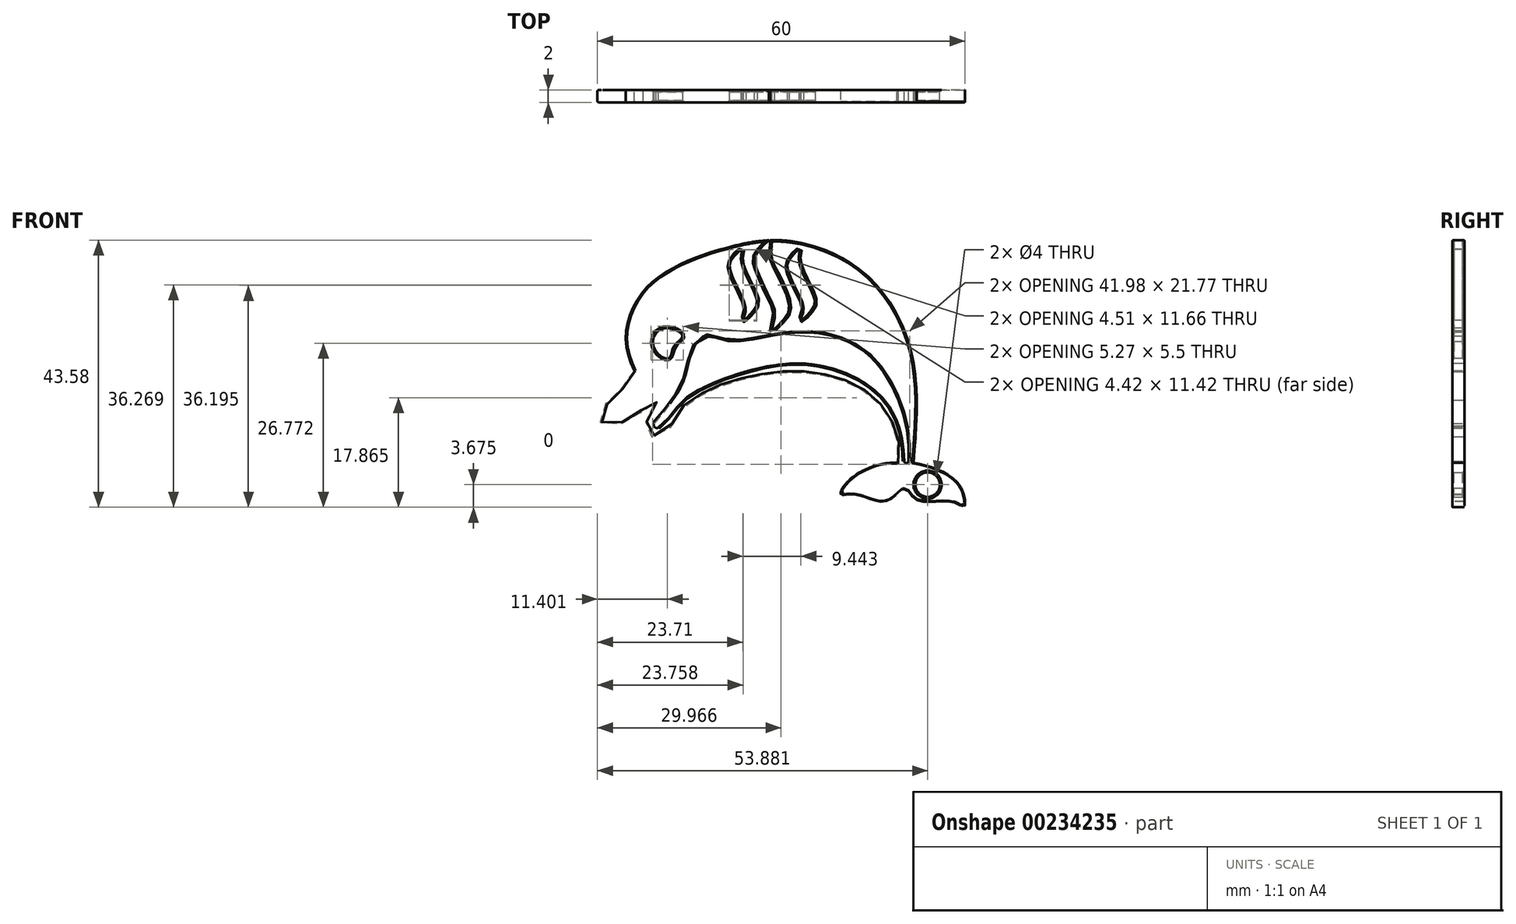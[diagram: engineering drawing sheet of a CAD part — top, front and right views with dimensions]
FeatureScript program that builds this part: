
annotation { "Feature Type Name" : "Feature", "Feature Type Description" : "" }
export const myFeature = defineFeature(function(context is Context, id is Id, definition is map)
    precondition{}
    {
        {
            var Q0;
            Q0=qCreatedBy(makeId("Front.planeOp"),FACE);
            var sketch = newSketch(context, id + "F0", { "sketchPlane" : qUnion([Q0])});
            skFitSpline(sketch, "E0", {"points": [v(-25.48, -7.62) * mm, v(-26.83, -2.44) * mm, v(-23.22, 6.13) * mm, v(-10.52, 12.36) * mm, v(0, 13.5) * mm, v(12.02, 8.3) * mm, v(19.83, -4.92) * mm, v(20.13, -22.67) * mm], "startDerivative": vector(-20.96, 49.8) * mm, "endDerivative": vector(-8.27, -104.1) * mm});
            skFitSpline(sketch, "E1", {"points": [v(20.13, -22.67) * mm, v(25.04, -24.25) * mm, v(28.1, -27.22) * mm, v(28.4, -29.9) * mm, v(26.81, -29.13) * mm, v(20.58, -28.67) * mm, v(18.7, -26.86) * mm, v(15.8, -28.9) * mm, v(10.31, -27.8) * mm, v(8.28, -27.87) * mm, v(9.54, -25.64) * mm, v(17.45, -22.67) * mm], "startDerivative": vector(47.96, -7.58) * mm, "endDerivative": vector(65.5, -3.83) * mm});
            skFitSpline(sketch, "E2", {"points": [v(17.45, -22.67) * mm, v(17.45, -18.89) * mm, v(13.41, -11.98) * mm, v(0.56, -7.9) * mm, v(-10.45, -9.84) * mm, v(-13.1, -10.91) * mm, v(-17.69, -13.98) * mm, v(-19.69, -17.15) * mm, v(-22.7, -18.48) * mm, v(-24.03, -17.48) * mm, v(-21.95, -12.6) * mm, v(-25.5, -15.24) * mm, v(-30.5, -16.46) * mm, v(-31.4, -14.6) * mm, v(-29.09, -12.24) * mm, v(-25.48, -7.62) * mm], "startDerivative": vector(8.68, 59.04) * mm, "endDerivative": vector(47.2, 70.58) * mm});
            skFitSpline(sketch, "E3", {"points": [v(-9.13, 12.73) * mm, v(-6.32, 19.23) * mm, v(-1.91, 23.13) * mm, v(0.96, 22.9) * mm, v(0, 20.55) * mm, v(0, 13.5) * mm], "startDerivative": vector(9.74, 28.22) * mm, "endDerivative": vector(4.25, -32.67) * mm});
            skFitSpline(sketch, "E4", {"points": [v(-19.86, -5.63) * mm, v(-22.28, -3.76) * mm, v(-20.8, -0.77) * mm, v(-17.55, -1.97) * mm, v(-18.89, -3.54) * mm, v(-19.86, -5.63) * mm]});
            skFitSpline(sketch, "E5", {"points": [v(-21.48, -16.92) * mm, v(-19.29, -14.65) * mm, v(-16.83, -11.98) * mm, v(-4.55, -7.12) * mm, v(6.9, -7.28) * mm, v(15.54, -12.61) * mm, v(18.6, -22.41) * mm], "startDerivative": vector(18.5, 14.45) * mm, "endDerivative": vector(1.69, -62.94) * mm});
            skFitSpline(sketch, "E6", {"points": [v(-22.23, -16.28) * mm, v(-17.9, -10.45) * mm, v(-16.42, -5.68) * mm, v(-14.3, -2.06) * mm, v(-9.93, -2.8) * mm, v(0, -1.47) * mm, v(12.5, -4.77) * mm, v(18.89, -16.33) * mm, v(19.3, -22.41) * mm], "startDerivative": vector(23.26, 24.72) * mm, "endDerivative": vector(-1, -48.83) * mm});
            skArc(sketch, "E7", {"start": v(-22.23, -16.28) * mm, "mid": v(-22.1, -16.88) * mm, "end": v(-21.48, -16.92) * mm});
            skArc(sketch, "E8", {"start": v(18.6, -22.41) * mm, "mid": v(18.95, -22.75) * mm, "end": v(19.3, -22.41) * mm});
            skCircle(sketch, "E9", {"center": v(22.43, -26.25) * mm, "radius": 2 * mm});
            skFitSpline(sketch, "E10", {"points": [v(-5.51, 11.36) * mm, v(-3.34, 13.68) * mm, v(-3.24, 13.56) * mm, v(-3.4, 12.14) * mm, v(-3.16, 10.16) * mm, v(-2.05, 7.9) * mm, v(-0.15, 3) * mm, v(-0.89, 0.9) * mm, v(-2.95, -1.08) * mm, v(-2.93, -0.69) * mm, v(-2.5, 1.69) * mm, v(-3.28, 4.04) * mm, v(-5.66, 9.5) * mm, v(-5.51, 11.36) * mm]});
            skFitSpline(sketch, "E11", {"points": [v(-9.69, 10.25) * mm, v(-8.42, 11.8) * mm, v(-7.87, 12.13) * mm, v(-8.04, 10.35) * mm, v(-5.44, 4.02) * mm, v(-6.07, 2.04) * mm, v(-7.64, 0.56) * mm, v(-7.59, 1.08) * mm, v(-7.25, 2.54) * mm, v(-8.57, 5.8) * mm, v(-9.89, 9.14) * mm, v(-9.69, 10.25) * mm]});
            skFitSpline(sketch, "E12", {"points": [v(-0.25, 10.27) * mm, v(1.03, 11.8) * mm, v(1.58, 12.14) * mm, v(1.4, 10.36) * mm, v(4, 4.03) * mm, v(3.37, 2.06) * mm, v(1.8, 0.57) * mm, v(1.85, 1.1) * mm, v(2.2, 2.56) * mm, v(0.88, 5.83) * mm, v(-0.45, 9.16) * mm, v(-0.25, 10.27) * mm]});
            skSolve(sketch);
        }
        {
            var Q0;
            Q0=makeQuery(id+"F0.imprint","IMPRINT",FACE,{"disambiguationData":[TD([[makeQuery(id+"F0.imprint","IMPRINT",EDGE,{"derivedFrom":sQuery(id+"F0.wireOp",EDGE,"E0")}),-1.0]])]});
            extrude(context, id + "F1", {"entities" : qUnion([Q0]), "depth" : 2 * mm});
        }
        {
            var Q0;
            Q0=makeQuery(id+"F1.opExtrude","CAP_EDGE",EDGE,{"disambiguationData":[OSD([sQuery(id+"F0.wireOp",EDGE,"E9")])],"isStart":false});
            var Q1;
            Q1=makeQuery(id+"F1.opExtrude","CAP_EDGE",EDGE,{"disambiguationData":[OSD([sQuery(id+"F0.wireOp",EDGE,"E9")])],"isStart":true});
            var Q2;
            Q2=makeQuery(id+"F1.opExtrude","CAP_EDGE",EDGE,{"disambiguationData":[OSD([sQuery(id+"F0.wireOp",EDGE,"E11")])],"isStart":false});
            var Q3;
            Q3=makeQuery(id+"F1.opExtrude","CAP_EDGE",EDGE,{"disambiguationData":[OSD([sQuery(id+"F0.wireOp",EDGE,"E10")])],"isStart":false});
            var Q4;
            Q4=makeQuery(id+"F1.opExtrude","CAP_EDGE",EDGE,{"disambiguationData":[OSD([sQuery(id+"F0.wireOp",EDGE,"E12")])],"isStart":false});
            var Q5;
            Q5=makeQuery(id+"F1.opExtrude","CAP_EDGE",EDGE,{"disambiguationData":[OSD([sQuery(id+"F0.wireOp",EDGE,"E12")])],"isStart":true});
            var Q6;
            Q6=makeQuery(id+"F1.opExtrude","CAP_EDGE",EDGE,{"disambiguationData":[OSD([sQuery(id+"F0.wireOp",EDGE,"E10")])],"isStart":true});
            var Q7;
            Q7=makeQuery(id+"F1.opExtrude","CAP_EDGE",EDGE,{"disambiguationData":[OSD([sQuery(id+"F0.wireOp",EDGE,"E11")])],"isStart":true});
            var Q8;
            Q8=makeQuery(id+"F1.opExtrude","CAP_EDGE",EDGE,{"disambiguationData":[OSD([sQuery(id+"F0.wireOp",EDGE,"E4")])],"isStart":true});
            var Q9;
            Q9=makeQuery(id+"F1.opExtrude","CAP_EDGE",EDGE,{"disambiguationData":[OSD([sQuery(id+"F0.wireOp",EDGE,"E4")])],"isStart":false});
            chamfer(context, id + "F2", {"entities" : qUnion([Q0, Q1, Q2, Q3, Q4, Q5, Q6, Q7, Q8, Q9]), "width" : .3 * mm, "tangentPropagation" : true});
        }
        {
            var Q0;
            Q0=makeQuery(id+"F1.opExtrude","CAP_EDGE",EDGE,{"disambiguationData":[OSD([sQuery(id+"F0.wireOp",EDGE,"E5")])],"isStart":false});
            var Q1;
            Q1=makeQuery(id+"F1.opExtrude","CAP_EDGE",EDGE,{"disambiguationData":[OSD([sQuery(id+"F0.wireOp",EDGE,"E6")])],"isStart":false});
            var Q2;
            Q2=makeQuery(id+"F1.opExtrude","CAP_EDGE",EDGE,{"disambiguationData":[OSD([sQuery(id+"F0.wireOp",EDGE,"E2")])],"isStart":false});
            var Q3;
            Q3=makeQuery(id+"F1.opExtrude","CAP_EDGE",EDGE,{"disambiguationData":[OSD([sQuery(id+"F0.wireOp",EDGE,"E0")])],"isStart":false});
            var Q4;
            Q4=makeQuery(id+"F1.opExtrude","CAP_EDGE",EDGE,{"disambiguationData":[OSD([sQuery(id+"F0.wireOp",EDGE,"E3")])],"isStart":false});
            var Q5;
            Q5=makeQuery(id+"F1.opExtrude","CAP_EDGE",EDGE,{"disambiguationData":[OSD([sQuery(id+"F0.wireOp",EDGE,"E0")])],"isStart":false});
            var Q6;
            Q6=makeQuery(id+"F1.opExtrude","CAP_EDGE",EDGE,{"disambiguationData":[OSD([sQuery(id+"F0.wireOp",EDGE,"E8")])],"isStart":false});
            var Q7;
            Q7=makeQuery(id+"F1.opExtrude","CAP_EDGE",EDGE,{"disambiguationData":[OSD([sQuery(id+"F0.wireOp",EDGE,"E0")])],"isStart":true});
            var Q8;
            Q8=makeQuery(id+"F1.opExtrude","CAP_EDGE",EDGE,{"disambiguationData":[OSD([sQuery(id+"F0.wireOp",EDGE,"E3")])],"isStart":true});
            var Q9;
            Q9=makeQuery(id+"F1.opExtrude","CAP_EDGE",EDGE,{"disambiguationData":[OSD([sQuery(id+"F0.wireOp",EDGE,"E0")])],"isStart":true});
            var Q10;
            Q10=makeQuery(id+"F1.opExtrude","CAP_EDGE",EDGE,{"disambiguationData":[OSD([sQuery(id+"F0.wireOp",EDGE,"E5")])],"isStart":true});
            var Q11;
            Q11=makeQuery(id+"F1.opExtrude","CAP_EDGE",EDGE,{"disambiguationData":[OSD([sQuery(id+"F0.wireOp",EDGE,"E6")])],"isStart":true});
            var Q12;
            Q12=makeQuery(id+"F1.opExtrude","CAP_EDGE",EDGE,{"disambiguationData":[OSD([sQuery(id+"F0.wireOp",EDGE,"E2")])],"isStart":true});
            fillet(context, id + "F3", {"entities" : qUnion([Q0, Q1, Q2, Q3, Q4, Q5, Q6, Q7, Q8, Q9, Q10, Q11, Q12]), "radius" : .2 * mm, "tangentPropagation" : true, "allowEdgeOverflow" : false});
        }
        {
            var Q0;
            Q0=makeQuery(id+"F1.opExtrude","CAP_EDGE",EDGE,{"disambiguationData":[OSD([sQuery(id+"F0.wireOp",EDGE,"E1")])],"isStart":false});
            var Q1;
            Q1=makeQuery(id+"F1.opExtrude","CAP_EDGE",EDGE,{"disambiguationData":[OSD([sQuery(id+"F0.wireOp",EDGE,"E1")])],"isStart":true});
            fillet(context, id + "F4", {"entities" : qUnion([Q0, Q1]), "radius" : .1 * mm, "tangentPropagation" : true, "allowEdgeOverflow" : false});
        }
    });
